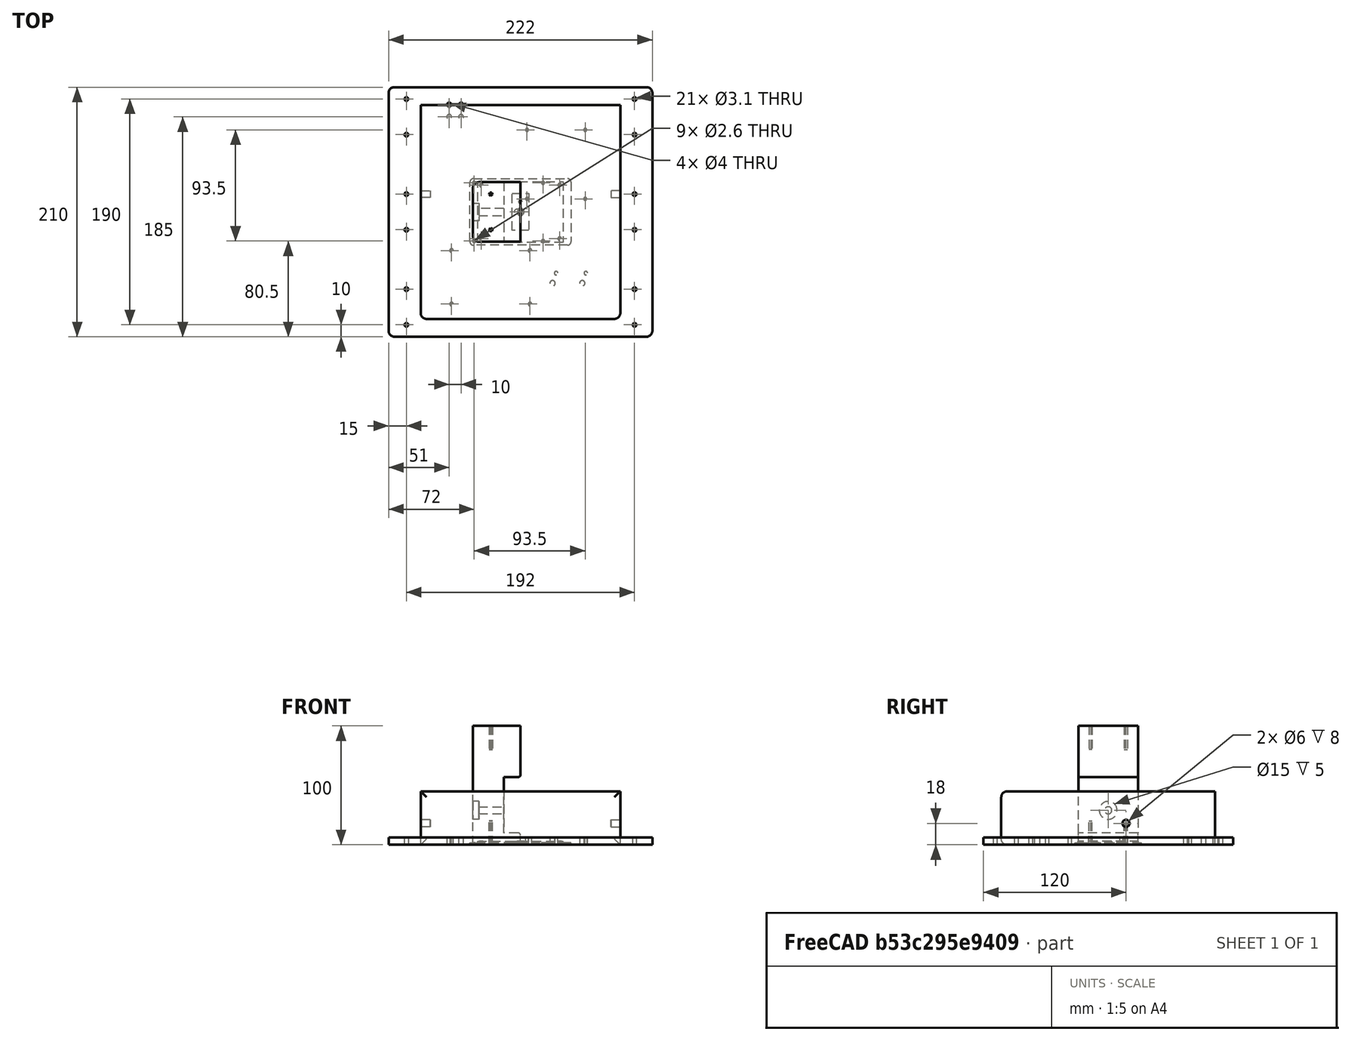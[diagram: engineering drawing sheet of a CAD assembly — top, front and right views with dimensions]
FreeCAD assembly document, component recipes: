
FREECAD ASSEMBLY — COMPONENT RECIPES ("case")

This assembly document has 11 components, labeled P0..P10 below (a component is one placed body or linked part). 10 of them carry a construction recipe — the FreeCAD feature program that regenerates the part from scratch, quoted from this document or its linked companion documents; the rest are supplied as boundary geometry only. No exploded tour is included for this assembly.
COMPONENT P0 — recipe-attached ("Upper_Panel", modeled in this document).
Construction recipe (the document's own serialized feature program — sketch geometry with constraints, then the solid features built on it; lengths are millimeters unless a unit is written):

FEATURE [PartDesign::FeatureBase] Clone
  BaseFeature = -> Lower_Panel
FEATURE [PartDesign::CoordinateSystem] Local_CS025
  AttacherType = Attacher::AttachEngine3D
  MapMode = 45
  Placement = pos=(-96,-80,0) rot=(0,0,1;0rad)
  Support = -> [Clone]
FEATURE [Sketcher::SketchObject] Sketch017
  AttachmentOffset = pos=(30,50,0) rot=(0,0,1;1.5708rad)
  FullyConstrained = true
  MapMode = 5
  Placement = pos=(30,50,0) rot=(0,0,1;1.5708rad)
  Support = -> [XY_Plane010]
  expr: .Constraints.hole_diameter = Sketch003.Constraints[3]
  expr: Constraints[34] = Sketch003.Constraints[34]
  expr: Constraints[36] = Sketch003.Constraints[36]
  expr: Constraints[12] = Sketch003.Constraints[12]
  expr: Constraints[13] = Sketch003.Constraints[13]
  expr: Constraints[31] = Sketch003.Constraints[31]
  expr: Constraints[35] = Sketch003.Constraints[35]
  sketch-geometry (16):
    g0: Circle CenterX=-39 CenterY=24.5 CenterZ=0 NormalX=0 NormalY=0 NormalZ=1 AngleXU=0 Radius=1.3
    g1: Circle CenterX=19 CenterY=24.5 CenterZ=0 NormalX=0 NormalY=0 NormalZ=1 AngleXU=0 Radius=1.3
    g2: Circle CenterX=-39 CenterY=-24.5 CenterZ=0 NormalX=0 NormalY=0 NormalZ=1 AngleXU=0 Radius=1.3
    g3: Circle CenterX=19 CenterY=-24.5 CenterZ=0 NormalX=0 NormalY=0 NormalZ=1 AngleXU=0 Radius=1.3
    g4: LineSegment StartX=-39 StartY=24.5 StartZ=0 EndX=19 EndY=24.5 EndZ=0
    g5: LineSegment StartX=19 StartY=24.5 StartZ=0 EndX=19 EndY=-24.5 EndZ=0
    g6: LineSegment StartX=19 StartY=-24.5 StartZ=0 EndX=-39 EndY=-24.5 EndZ=0
    g7: LineSegment StartX=-39 StartY=-24.5 StartZ=0 EndX=-39 EndY=24.5 EndZ=0
    g8: LineSegment StartX=-39.5 StartY=28 StartZ=0 EndX=39.5 EndY=28 EndZ=0
    g9: LineSegment StartX=42.5 StartY=25 StartZ=0 EndX=42.5 EndY=-25 EndZ=0
    g10: LineSegment StartX=39.5 StartY=-28 StartZ=0 EndX=-39.5 EndY=-28 EndZ=0
    g11: LineSegment StartX=-42.5 StartY=-25 StartZ=0 EndX=-42.5 EndY=25 EndZ=0
    g12: ArcOfCircle CenterX=-39.5 CenterY=25 CenterZ=0 NormalX=0 NormalY=0 NormalZ=1 AngleXU=0 Radius=3 StartAngle=1.5708 EndAngle=3.14159
    g13: ArcOfCircle CenterX=-39.5 CenterY=-25 CenterZ=0 NormalX=0 NormalY=0 NormalZ=1 AngleXU=0 Radius=3 StartAngle=3.14159 EndAngle=4.71239
    g14: ArcOfCircle CenterX=39.5 CenterY=-25 CenterZ=0 NormalX=0 NormalY=0 NormalZ=1 AngleXU=0 Radius=3 StartAngle=4.71239 EndAngle=6.28319
    g15: ArcOfCircle CenterX=39.5 CenterY=25 CenterZ=0 NormalX=0 NormalY=0 NormalZ=1 AngleXU=0 Radius=3 StartAngle=0 EndAngle=1.5708
  constraints (37):
    c: Equal(g0,g1)
    c: Equal(g1,g2)
    c: Equal(g2,g3)
    c: Diameter(g1) = 2.6  'hole_diameter'
    c: Coincident(g4,g5)
    c: Coincident(g5,g6)
    c: Coincident(g6,g7)
    c: Coincident(g7,g4)
    c: Horizontal(g4)
    c: Horizontal(g6)
    c: Vertical(g5)
    c: Symmetric(g4,g6,g-1)
    c: DistanceY(g7,g7) = 49
    c: DistanceX(g4,g4) = 58
    c: Coincident(g1,g4)
    c: Coincident(g3,g5)
    c: Coincident(g4,g0)
    c: Coincident(g6,g2)
    c: Horizontal(g8)
    c: Horizontal(g10)
    c: Vertical(g9)
    c: Vertical(g11)
    c: Tangent(g8,g12) = 1.5708
    c: Tangent(g11,g12) = 1.5708
    c: Tangent(g11,g13) = 1.5708
    c: Tangent(g10,g13) = 1.5708
    c: Tangent(g10,g14) = 1.5708
    c: Tangent(g9,g14) = 1.5708
    c: Tangent(g9,g15) = 1.5708
    c: Tangent(g8,g15) = 1.5708
    c: Equal(g13,g14)
    c: Radius(g15) = 3
    c: Symmetric(g8,g10,g-1)
    c: Symmetric(g11,g9,g-2)
    c: DistanceX(g11,g9) = 85
    c: DistanceY(g10,g8) = 56
    c: DistanceX(g11,g2) = 3.5
FEATURE [PartDesign::Pocket] Pocket009  label="Upper_Panel_Pi_Mounting_Holes"
  BaseFeature = -> Clone
  Length = 5
  Length2 = 100
  Profile = -> Sketch017
  Reversed = true
  Type = 1
FEATURE [PartDesign::CoordinateSystem] Local_CS026  label="Upper_Panel_Pi_Mounting_Hole_1"
  AttacherType = Attacher::AttachEngine3D
  AttachmentOffset = pos=(0,0,0) rot=(1,0,0;3.14159rad)
  MapMode = 45
  Placement = pos=(5.5,11,0) rot=(0.70712,0.707094,0;3.14159rad)
  Support = -> [Pocket009]
FEATURE [PartDesign::CoordinateSystem] Local_CS027  label="Upper_Panel_Pi_Mounting_Hole_2"
  AttacherType = Attacher::AttachEngine3D
  AttachmentOffset = pos=(0,0,0) rot=(1,0,0;3.14159rad)
  MapMode = 45
  Placement = pos=(54.5,11,0) rot=(0.70708,0.707133,0;3.14159rad)
  Support = -> [Pocket009]
FEATURE [PartDesign::CoordinateSystem] Local_CS028  label="Upper_Panel_Pi_Mounting_Hole_3"
  AttacherType = Attacher::AttachEngine3D
  AttachmentOffset = pos=(0,0,0) rot=(1,0,0;3.14159rad)
  MapMode = 45
  Placement = pos=(5.5,69,0) rot=(0.7071,0.707113,0;3.14159rad)
  Support = -> [Pocket009]
FEATURE [PartDesign::CoordinateSystem] Local_CS029  label="Upper_Panel_Pi_Mounting_Hole_4"
  AttacherType = Attacher::AttachEngine3D
  AttachmentOffset = pos=(0,0,0) rot=(1,0,0;3.14159rad)
  MapMode = 45
  Placement = pos=(54.5,69,0) rot=(0.707107,0.707107,0;3.14159rad)
  Support = -> [Pocket009]
FEATURE [Sketcher::SketchObject] Sketch018
  AttachmentOffset = pos=(-25,-55,0) rot=(0,0,1;0rad)
  FullyConstrained = true
  MapMode = 5
  Placement = pos=(-25,-55,0) rot=(0,0,1;0rad)
  Support = -> [XY_Plane010]
  expr: .Constraints.hole_diameter = Sketch001.Constraints[3]
  expr: Constraints[16] = Sketch001.Constraints[16]
  expr: Constraints[17] = Sketch001.Constraints[17]
  sketch-geometry (8):
    g0: Circle CenterX=-33 CenterY=22.5 CenterZ=0 NormalX=0 NormalY=0 NormalZ=1 AngleXU=0 Radius=1.55
    g1: Circle CenterX=33 CenterY=22.5 CenterZ=0 NormalX=0 NormalY=0 NormalZ=1 AngleXU=0 Radius=1.55
    g2: Circle CenterX=-33 CenterY=-22.5 CenterZ=0 NormalX=0 NormalY=0 NormalZ=1 AngleXU=0 Radius=1.55
    g3: Circle CenterX=33 CenterY=-22.5 CenterZ=0 NormalX=0 NormalY=0 NormalZ=1 AngleXU=0 Radius=1.55
    g4: LineSegment StartX=-33 StartY=22.5 StartZ=0 EndX=33 EndY=22.5 EndZ=0
    g5: LineSegment StartX=33 StartY=22.5 StartZ=0 EndX=33 EndY=-22.5 EndZ=0
    g6: LineSegment StartX=33 StartY=-22.5 StartZ=0 EndX=-33 EndY=-22.5 EndZ=0
    g7: LineSegment StartX=-33 StartY=-22.5 StartZ=0 EndX=-33 EndY=22.5 EndZ=0
  constraints (18):
    c: Equal(g0,g1)
    c: Equal(g1,g2)
    c: Equal(g2,g3)
    c: Diameter(g1) = 3.1  'hole_diameter'
    c: Coincident(g4,g5)
    c: Coincident(g5,g6)
    c: Coincident(g6,g7)
    c: Coincident(g7,g4)
    c: Horizontal(g6)
    c: Vertical(g5)
    c: Symmetric(g4,g6,g-1)
    c: Symmetric(g4,g4,g-2)
    c: Coincident(g0,g4)
    c: Coincident(g2,g6)
    c: Coincident(g1,g4)
    c: Coincident(g3,g5)
    c: DistanceX(g4,g4) = 66
    c: DistanceY(g7,g7) = 45
FEATURE [PartDesign::Pocket] Pocket010  label="Upper_Panel_Relay_Mounting_Holes"
  BaseFeature = -> Pocket009
  Length = 5
  Length2 = 100
  Profile = -> Sketch018
  Reversed = true
  Type = 1
FEATURE [PartDesign::CoordinateSystem] Local_CS030  label="Upper_Panel_Relay_Mounting_Hole_1"
  AttacherType = Attacher::AttachEngine3D
  AttachmentOffset = pos=(0,0,0) rot=(1,0,0;3.14159rad)
  MapMode = 45
  Placement = pos=(8,-77.5,0) rot=(1,6e-06,0;3.14159rad)
  Support = -> [Pocket010]
FEATURE [PartDesign::CoordinateSystem] Local_CS031  label="Upper_Panel_Relay_Mounting_Hole_2"
  AttacherType = Attacher::AttachEngine3D
  AttachmentOffset = pos=(0,0,0) rot=(1,0,0;3.14159rad)
  MapMode = 45
  Placement = pos=(8,-32.5,0) rot=(1,0,0;3.14159rad)
  Support = -> [Pocket010]
FEATURE [PartDesign::CoordinateSystem] Local_CS032  label="Upper_Panel_Relay_Mounting_Hole_3"
  AttacherType = Attacher::AttachEngine3D
  AttachmentOffset = pos=(0,0,0) rot=(1,0,0;3.14159rad)
  MapMode = 45
  Placement = pos=(-58,-77.5,0) rot=(1,-4.4e-05,0;3.14159rad)
  Support = -> [Pocket010]
FEATURE [PartDesign::CoordinateSystem] Local_CS033  label="Upper_Panel_Relay_Mounting_Hole_4"
  AttacherType = Attacher::AttachEngine3D
  AttachmentOffset = pos=(0,0,0) rot=(1,0,0;3.14159rad)
  MapMode = 45
  Placement = pos=(-58,-32.5,0) rot=(1,0,0;3.14159rad)
  Support = -> [Pocket010]
FEATURE [Sketcher::SketchObject] Sketch019
  FullyConstrained = true
  MapMode = 5
  Support = -> [XY_Plane010]
  expr: Constraints[18] = <<Lower_Panel_Outline>>.Constraints.depth / 2 - 15mm
  sketch-geometry (8):
    g0: Circle CenterX=-60 CenterY=90 CenterZ=0 NormalX=0 NormalY=0 NormalZ=1 AngleXU=0 Radius=2
    g1: Circle CenterX=-50 CenterY=90 CenterZ=0 NormalX=0 NormalY=0 NormalZ=1 AngleXU=0 Radius=2
    g2: Circle CenterX=-60 CenterY=80 CenterZ=0 NormalX=0 NormalY=0 NormalZ=1 AngleXU=0 Radius=2
    g3: Circle CenterX=-50 CenterY=80 CenterZ=0 NormalX=0 NormalY=0 NormalZ=1 AngleXU=0 Radius=2
    g4: LineSegment StartX=-60 StartY=90 StartZ=0 EndX=-50 EndY=90 EndZ=0
    g5: LineSegment StartX=-50 StartY=90 StartZ=0 EndX=-50 EndY=80 EndZ=0
    g6: LineSegment StartX=-50 StartY=80 StartZ=0 EndX=-60 EndY=80 EndZ=0
    g7: LineSegment StartX=-60 StartY=80 StartZ=0 EndX=-60 EndY=90 EndZ=0
  constraints (20):
    c: Equal(g0,g1)
    c: Equal(g1,g2)
    c: Equal(g2,g3)
    c: Coincident(g4,g5)
    c: Coincident(g5,g6)
    c: Coincident(g6,g7)
    c: Coincident(g7,g4)
    c: Horizontal(g4)
    c: Horizontal(g6)
    c: Vertical(g5)
    c: Vertical(g7)
    c: Coincident(g0,g4)
    c: Coincident(g4,g1)
    c: Coincident(g6,g2)
    c: Coincident(g5,g3)
    c: Diameter(g1) = 4
    c: Equal(g4,g7)
    c: DistanceY(g7,g7) = 10
    c: DistanceY(g-1,g1) = 90
    c: DistanceX(g3,g-1) = 50
FEATURE [PartDesign::Pocket] Pocket011  label="Upper_Panel_Cable_Clamp"
  BaseFeature = -> Pocket010
  Length = 5
  Length2 = 100
  Profile = -> Sketch019
  Reversed = true
  Type = 1
FEATURE [Sketcher::SketchObject] Sketch023  label="Photosensor_PCB_Mount_S"
  AttachmentOffset = pos=(30,-60,0) rot=(0,0,1;0rad)
  FullyConstrained = true
  MapMode = 5
  Placement = pos=(30,-60,0) rot=(0,0,1;0rad)
  Support = -> [XY_Plane010]
  expr: Constraints[24] = Sketch022.Constraints[11]
  expr: Constraints[25] = Sketch022.Constraints[12]
  expr: Constraints[21] = Sketch022.Constraints[8]
  expr: .Constraints.diameter = Sketch021.Constraints[12]
  expr: Constraints[11] = Sketch021.Constraints[11]
  expr: Constraints[22] = Sketch022.Constraints[9]
  expr: Constraints[9] = Sketch021.Constraints[9]
  expr: Constraints[8] = Sketch021.Constraints[8]
  sketch-geometry (10):
    g0: LineSegment StartX=-7 StartY=15.5 StartZ=0 EndX=7 EndY=15.5 EndZ=0
    g1: LineSegment StartX=7 StartY=15.5 StartZ=0 EndX=7 EndY=-15.5 EndZ=0
    g2: LineSegment StartX=7 StartY=-15.5 StartZ=0 EndX=-7 EndY=-15.5 EndZ=0
    g3: LineSegment StartX=-7 StartY=-15.5 StartZ=0 EndX=-7 EndY=15.5 EndZ=0
    g4: Circle CenterX=0 CenterY=8.5 CenterZ=0 NormalX=0 NormalY=0 NormalZ=1 AngleXU=0 Radius=1.5
    g5: LineSegment StartX=-7 StartY=15.5 StartZ=0 EndX=7 EndY=15.5 EndZ=0
    g6: LineSegment StartX=7 StartY=15.5 StartZ=0 EndX=7 EndY=-15.5 EndZ=0
    g7: LineSegment StartX=7 StartY=-15.5 StartZ=0 EndX=-7 EndY=-15.5 EndZ=0
    g8: LineSegment StartX=-7 StartY=-15.5 StartZ=0 EndX=-7 EndY=15.5 EndZ=0
    g9: Circle CenterX=-3 CenterY=0 CenterZ=0 NormalX=0 NormalY=0 NormalZ=1 AngleXU=0 Radius=2.25
  constraints (26):
    c: Coincident(g0,g1)
    c: Coincident(g1,g2)
    c: Coincident(g2,g3)
    c: Coincident(g3,g0)
    c: Horizontal(g2)
    c: Vertical(g1)
    c: Symmetric(g0,g0,g-2)
    c: Symmetric(g0,g2,g-1)
    c: DistanceX(g0,g0) = 14
    c: DistanceY(g1,g1) = 31
    c: PointOnObject(g4,g-2)
    c: DistanceY(g4,g0) = 7
    c: Diameter(g4) = 3  'diameter'
    c: Coincident(g5,g6)
    c: Coincident(g6,g7)
    c: Coincident(g7,g8)
    c: Coincident(g8,g5)
    c: Horizontal(g7)
    c: Vertical(g6)
    c: Symmetric(g5,g5,g-2)
    c: Symmetric(g5,g7,g-1)
    c: DistanceX(g5,g5) = 14
    c: DistanceY(g6,g6) = 31
    c: PointOnObject(g9,g-1)
    c: DistanceX(g9,g-1) = 3
    c: Diameter(g9) = 4.5
FEATURE [PartDesign::Pocket] Pocket013  label="Photosensor_PCB_Mount"
  BaseFeature = -> Pocket011
  Length = 0
  Length2 = 100
  Profile = -> Sketch023
  Reversed = true
  Type = 1
FEATURE [PartDesign::LinearPattern] LinearPattern  label="Photosensor_PCB_Mounts"
  BaseFeature = -> Pocket013
  Direction = -> Sketch023 [H_Axis]
  Length = 25
  Occurrences = 2
  Originals = -> [Pocket013]
FEATURE [PartDesign::CoordinateSystem] Local_CS035  label="Photosensor_PCB_1_Mounting_Hole"
  AttacherType = Attacher::AttachEngine3D
  MapMode = 45
  Placement = pos=(30,-51.5,0) rot=(0,0,1;0rad)
  Support = -> [LinearPattern]
FEATURE [PartDesign::CoordinateSystem] Local_CS036  label="Photosensor_PCB_2_Mounting_Hole"
  AttacherType = Attacher::AttachEngine3D
  MapMode = 45
  Placement = pos=(55,-51.5,0) rot=(0,0,1;0rad)
  Support = -> [LinearPattern]
FEATURE [PartDesign::Body] Body  label="Upper_Panel"
  BaseFeature = -> Lower_Panel
  Group = -> [Clone,Local_CS025,Sketch017,Pocket009,Local_CS026,Local_CS027,Local_CS028,Local_CS029,Sketch018,Pocket010,Local_CS030,Local_CS031,Local_CS032,Local_CS033,Sketch019,Pocket011,Sketch023,Pocket013,LinearPattern,Local_CS035,Local_CS036]
  Origin = -> Origin010
  Tip = -> LinearPattern
COMPONENT P1 — recipe-attached ("Pillar_Radio_Mount", modeled in this document).
Construction recipe (the document's own serialized feature program — sketch geometry with constraints, then the solid features built on it; lengths are millimeters unless a unit is written):

FEATURE [PartDesign::FeatureBase] Clone001
  BaseFeature = -> Corner_Pillar
FEATURE [Sketcher::SketchObject] Sketch024
  FullyConstrained = true
  MapMode = 5
  Placement = pos=(0,0,0) rot=(0.57735,0.57735,0.57735;2.0944rad)
  Support = -> [YZ_Plane013]
  sketch-geometry (1):
    g0: Circle CenterX=0 CenterY=29 CenterZ=0 NormalX=0 NormalY=0 NormalZ=1 AngleXU=0 Radius=3
  constraints (3):
    c: PointOnObject(g0,g-2)
    c: Diameter(g0) = 6
    c: DistanceY(g-1,g0) = 29
FEATURE [PartDesign::Plane] DatumPlane006  label="Pillar_Radio_Mount_Outer_Face"
  AttachmentOffset = pos=(0,0,-40) rot=(0,0,1;0rad)
  Length = 65.8114
  MapMode = 5
  Placement = pos=(-40,8.9e-15,-8.9e-15) rot=(0.57735,0.57735,0.57735;2.0944rad)
  ResizeMode = 0
  Support = -> [YZ_Plane013]
  Width = 140.811
  expr: .AttachmentOffset.Base.z = -<<Sketch010>>.Constraints.width
FEATURE [PartDesign::Pocket] Pocket014  label="Pillar_Radio_Mount_Hole"
  BaseFeature = -> Clone001
  Length = 0
  Length2 = 100
  Profile = -> Sketch024
  Type = 3
  UpToFace = -> DatumPlane006 [Plane]
FEATURE [PartDesign::CoordinateSystem] Local_CS037  label="Pillar_Radio_Mount_Hole_Pos"
  AttacherType = Attacher::AttachEngine3D
  MapMode = 45
  Placement = pos=(-14,2.37e-14,29) rot=(0.57735,0.57735,0.57735;2.0944rad)
  Support = -> [Pocket014]
FEATURE [Sketcher::SketchObject] Sketch025
  ExternalGeometry = -> [Pocket014]
  FullyConstrained = true
  MapMode = 5
  Placement = pos=(-40,8.9e-15,-8.9e-15) rot=(0.57735,0.57735,0.57735;2.0944rad)
  Support = -> [DatumPlane006]
  sketch-geometry (1):
    g0: Circle CenterX=8.9e-15 CenterY=29 CenterZ=0 NormalX=0 NormalY=0 NormalZ=1 AngleXU=0 Radius=7.5
  constraints (2):
    c: Coincident(g0,g-3)
    c: Diameter(g0) = 15
FEATURE [PartDesign::Pocket] Pocket015  label="Pillar_Radio_Mount_Hole_Recess"
  BaseFeature = -> Pocket014
  Length = 5
  Length2 = 100
  Profile = -> Sketch025
  Reversed = true
  Type = 0
FEATURE [PartDesign::CoordinateSystem] Local_CS038  label="Pillar_Radio_Mount_Mounting_Holes_Bottom_Pos"
  AttacherType = Attacher::AttachEngine3D
  AttachmentOffset = pos=(0,0,0) rot=(0,0.707107,0.707107;3.14159rad)
  MapMode = 45
  Placement = pos=(-25,0,0) rot=(0,0,1;0rad)
  Support = -> [Pocket015]
FEATURE [PartDesign::Body] Body001  label="Pillar_Radio_Mount"
  BaseFeature = -> Corner_Pillar
  Group = -> [Clone001,DatumPlane006,Sketch024,Pocket014,Local_CS037,Sketch025,Pocket015,Local_CS038]
  Origin = -> Origin013
  Tip = -> Pocket015
COMPONENT P2 — recipe-attached ("Pillar", modeled in this document).
Construction recipe (the document's own serialized feature program — sketch geometry with constraints, then the solid features built on it; lengths are millimeters unless a unit is written):

FEATURE [Sketcher::SketchObject] Sketch010
  FullyConstrained = true
  MapMode = 5
  Support = -> [XY_Plane008]
  expr: Constraints[9] = <<Lower_Panel_Outline>>.Constraints.corner_radius
  sketch-geometry (6):
    g0: LineSegment StartX=-35 StartY=25 StartZ=0 EndX=0 EndY=25 EndZ=0
    g1: LineSegment StartX=0 StartY=25 StartZ=0 EndX=0 EndY=-25 EndZ=0
    g2: LineSegment StartX=0 StartY=-25 StartZ=0 EndX=-35 EndY=-25 EndZ=0
    g3: LineSegment StartX=-40 StartY=-20 StartZ=0 EndX=-40 EndY=20 EndZ=0
    g4: ArcOfCircle CenterX=-35 CenterY=20 CenterZ=0 NormalX=0 NormalY=0 NormalZ=1 AngleXU=0 Radius=5 StartAngle=1.5708 EndAngle=3.14159
    g5: ArcOfCircle CenterX=-35 CenterY=-20 CenterZ=0 NormalX=0 NormalY=0 NormalZ=1 AngleXU=0 Radius=5 StartAngle=3.14159 EndAngle=4.71239
  constraints (15):
    c: Coincident(g0,g1)
    c: Coincident(g1,g2)
    c: Horizontal(g2)
    c: Vertical(g3)
    c: Tangent(g0,g4) = 1.5708
    c: Tangent(g3,g4) = 1.5708
    c: Tangent(g3,g5) = 1.5708
    c: Tangent(g2,g5) = 1.5708
    c: Equal(g4,g5)
    c: Radius(g4) = 5
    c: Symmetric(g0,g1,g-1)
    c: DistanceY(g1,g1) = 50  'depth'
    c: DistanceX(g3,g1) = 40  'width'
    c: PointOnObject(g1,g-2)
    c: Horizontal(g0)
FEATURE [PartDesign::Plane] DatumPlane003  label="Pillar_Top_Face"
  AttachmentOffset = pos=(0,0,100) rot=(0,0,1;0rad)
  Length = 76.4018
  MapMode = 5
  Placement = pos=(0,0,100) rot=(0,0,1;0rad)
  ResizeMode = 0
  Support = -> [XY_Plane008]
  Width = 61.4018
FEATURE [PartDesign::Pad] Pad007  label="Pillar_Body"
  Direction = (1,1,1)
  Length = 10
  Length2 = 100
  Profile = -> Sketch010
  Type = 3
  UpToFace = -> DatumPlane003 [Plane]
FEATURE [Sketcher::SketchObject] Sketch011
  ExternalGeometry = -> [Pad007]
  FullyConstrained = true
  MapMode = 5
  Placement = pos=(0,0,0) rot=(0.57735,0.57735,0.57735;2.0944rad)
  Support = -> [YZ_Plane008]
  expr: Constraints[11] = <<Motorola_GM900_Body>>.Length + 2mm
  sketch-geometry (4):
    g0: LineSegment StartX=-25 StartY=57 StartZ=0 EndX=25 EndY=57 EndZ=0
    g1: LineSegment StartX=25 StartY=57 StartZ=0 EndX=25 EndY=10 EndZ=0
    g2: LineSegment StartX=25 StartY=10 StartZ=0 EndX=-25 EndY=10 EndZ=0
    g3: LineSegment StartX=-25 StartY=10 StartZ=0 EndX=-25 EndY=57 EndZ=0
  constraints (13):
    c: Coincident(g0,g1)
    c: Coincident(g1,g2)
    c: Coincident(g2,g3)
    c: Coincident(g3,g0)
    c: Horizontal(g0)
    c: Horizontal(g2)
    c: Vertical(g1)
    c: Vertical(g3)
    c: PointOnObject(g0,g-3)
    c: PointOnObject(g0,g-4)
    c: DistanceY(g-1,g1) = 10  'lower_y_offset'
    c: DistanceY(g3,g3) = 47
    c: DistanceY(g0,g-4) = 43
FEATURE [PartDesign::Pocket] Pocket003  label="Pillar_Radio_Cutout"
  BaseFeature = -> Pad007
  Length = 14
  Length2 = 100
  Profile = -> Sketch011
  Type = 0
FEATURE [Sketcher::SketchObject] Sketch012
  ExternalGeometry = -> [Sketch010]
  FullyConstrained = true
  MapMode = 5
  Support = -> [XY_Plane008]
  sketch-geometry (13):
    g0: LineSegment StartX=-25 StartY=15 StartZ=0 EndX=-25 EndY=-15 EndZ=0
    g1: LineSegment StartX=-25 StartY=13.475 StartZ=0 EndX=-23.5496 EndY=14.5287 EndZ=0
    g2: LineSegment StartX=-23.5496 StartY=14.5287 StartZ=0 EndX=-24.1036 EndY=16.2338 EndZ=0
    g3: LineSegment StartX=-24.1036 StartY=16.2338 StartZ=0 EndX=-25.8964 EndY=16.2338 EndZ=0
    g4: LineSegment StartX=-25.8964 StartY=16.2338 StartZ=0 EndX=-26.4504 EndY=14.5287 EndZ=0
    g5: LineSegment StartX=-26.4504 StartY=14.5287 StartZ=0 EndX=-25 EndY=13.475 EndZ=0
    g6: Circle CenterX=-25 CenterY=15 CenterZ=0 NormalX=0 NormalY=0 NormalZ=1 AngleXU=0 Radius=1.525
    g7: LineSegment StartX=-25 StartY=-13.475 StartZ=0 EndX=-26.4504 EndY=-14.5287 EndZ=0
    g8: LineSegment StartX=-26.4504 StartY=-14.5287 StartZ=0 EndX=-25.8964 EndY=-16.2338 EndZ=0
    g9: LineSegment StartX=-25.8964 StartY=-16.2338 StartZ=0 EndX=-24.1036 EndY=-16.2338 EndZ=0
    g10: LineSegment StartX=-24.1036 StartY=-16.2338 StartZ=0 EndX=-23.5496 EndY=-14.5287 EndZ=0
    g11: LineSegment StartX=-23.5496 StartY=-14.5287 StartZ=0 EndX=-25 EndY=-13.475 EndZ=0
    g12: Circle CenterX=-25 CenterY=-15 CenterZ=0 NormalX=0 NormalY=0 NormalZ=1 AngleXU=0 Radius=1.525
  constraints (33):
    c: DistanceY(g0,g0) = 30  'between_centres'
    c: DistanceX(g-3,g0) = 10
    c: Symmetric(g0,g0,g-1)
    c: Coincident(g1,g2)
    c: Coincident(g2,g3)
    c: Coincident(g3,g4)
    c: Coincident(g4,g5)
    c: Coincident(g5,g1)
    c: Equal(g1, g2-g5) x4
    c: PointOnObject(g1,g6)
    c: PointOnObject(g2,g6)
    c: PointOnObject(g3,g6)
    c: PointOnObject(g4,g6)
    c: PointOnObject(g5,g6)
    c: Coincident(g6,g0)
    c: PointOnObject(g5,g0)
    c: Coincident(g7,g8)
    c: Coincident(g8,g9)
    c: Coincident(g9,g10)
    c: Coincident(g10,g11)
    c: Coincident(g11,g7)
    c: Equal(g7, g8-g11) x4
    c: PointOnObject(g7,g12)
    c: PointOnObject(g8,g12)
    c: PointOnObject(g9,g12)
    c: PointOnObject(g10,g12)
    c: PointOnObject(g11,g12)
    c: Coincident(g12,g0)
    c: PointOnObject(g11,g0)
    c: Equal(g6,g12)
    c: Diameter(g6) = 3.05
    c: DistanceX(g-5,g0) = 15  'x_offset'
    c: DistanceY(g-6,g0) = 10  'y_offset'
FEATURE [Sketcher::SketchObject] Sketch013
  ExternalGeometry = -> [Sketch010]
  FullyConstrained = true
  MapMode = 5
  Placement = pos=(0,0,100) rot=(0,0,1;0rad)
  Support = -> [DatumPlane003]
  expr: Constraints[38] = Sketch012.Constraints[36]
  expr: Constraints[3] = Sketch012.Constraints[1]
  expr: Constraints[0] = Sketch012.Constraints.between_centres
  sketch-geometry (13):
    g0: LineSegment StartX=-25 StartY=15 StartZ=0 EndX=-25 EndY=-15 EndZ=0
    g1: LineSegment StartX=-25 StartY=13.475 StartZ=0 EndX=-23.5496 EndY=14.5287 EndZ=0
    g2: LineSegment StartX=-23.5496 StartY=14.5287 StartZ=0 EndX=-24.1036 EndY=16.2338 EndZ=0
    g3: LineSegment StartX=-24.1036 StartY=16.2338 StartZ=0 EndX=-25.8964 EndY=16.2338 EndZ=0
    g4: LineSegment StartX=-25.8964 StartY=16.2338 StartZ=0 EndX=-26.4504 EndY=14.5287 EndZ=0
    g5: LineSegment StartX=-26.4504 StartY=14.5287 StartZ=0 EndX=-25 EndY=13.475 EndZ=0
    g6: Circle CenterX=-25 CenterY=15 CenterZ=0 NormalX=0 NormalY=0 NormalZ=1 AngleXU=0 Radius=1.525
    g7: LineSegment StartX=-25 StartY=-13.475 StartZ=0 EndX=-26.4504 EndY=-14.5287 EndZ=0
    g8: LineSegment StartX=-26.4504 StartY=-14.5287 StartZ=0 EndX=-25.8964 EndY=-16.2338 EndZ=0
    g9: LineSegment StartX=-25.8964 StartY=-16.2338 StartZ=0 EndX=-24.1036 EndY=-16.2338 EndZ=0
    g10: LineSegment StartX=-24.1036 StartY=-16.2338 StartZ=0 EndX=-23.5496 EndY=-14.5287 EndZ=0
    g11: LineSegment StartX=-23.5496 StartY=-14.5287 StartZ=0 EndX=-25 EndY=-13.475 EndZ=0
    g12: Circle CenterX=-25 CenterY=-15 CenterZ=0 NormalX=0 NormalY=0 NormalZ=1 AngleXU=0 Radius=1.525
  constraints (33):
    c: DistanceY(g0,g0) = 30
    c: DistanceY(g-5,g0) = 5
    c: DistanceY(g0,g-3) = 5
    c: DistanceX(g-3,g0) = 10
    c: Symmetric(g0,g0,g-1)
    c: Coincident(g1,g2)
    c: Coincident(g2,g3)
    c: Coincident(g3,g4)
    c: Coincident(g4,g5)
    c: Coincident(g5,g1)
    c: Equal(g1, g2-g5) x4
    c: PointOnObject(g1,g6)
    c: PointOnObject(g2,g6)
    c: PointOnObject(g3,g6)
    c: PointOnObject(g4,g6)
    c: PointOnObject(g5,g6)
    c: Coincident(g6,g0)
    c: PointOnObject(g5,g0)
    c: Coincident(g7,g8)
    c: Coincident(g8,g9)
    c: Coincident(g9,g10)
    c: Coincident(g10,g11)
    c: Coincident(g11,g7)
    c: Equal(g7, g8-g11) x4
    c: PointOnObject(g7,g12)
    c: PointOnObject(g8,g12)
    c: PointOnObject(g9,g12)
    c: PointOnObject(g10,g12)
    c: PointOnObject(g11,g12)
    c: Coincident(g12,g0)
    c: PointOnObject(g11,g0)
    c: Equal(g6,g12)
    c: Diameter(g6) = 3.05
FEATURE [PartDesign::Fillet] Fillet  label="Pillar_Radio_Cutout_Rounding"
  Base = -> Pocket003 [Edge28,Edge23]
  BaseFeature = -> Pocket003
  Radius = 2
  SupportTransform = false
FEATURE [PartDesign::Pocket] Pocket004  label="Pillar_Bottom_Holes"
  BaseFeature = -> Fillet
  Length = 20
  Length2 = 100
  Profile = -> Sketch012
  Reversed = true
  Type = 0
FEATURE [PartDesign::Pocket] Pocket005  label="Pillar_Top_Holes"
  BaseFeature = -> Pocket004
  Length = 20
  Length2 = 100
  Profile = -> Sketch013
  Type = 0
  expr: Length = Pocket004.Length
FEATURE [PartDesign::CoordinateSystem] Local_CS014  label="Pillar_Mounting_Holes_Top_Pos"
  AttacherType = Attacher::AttachEngine3D
  AttachmentOffset = pos=(0,0,0) rot=(0,0.707107,0.707107;3.14159rad)
  MapMode = 45
  Placement = pos=(-25,0,100) rot=(0,0,1;0rad)
  Support = -> [Pocket005]
FEATURE [PartDesign::CoordinateSystem] Local_CS016  label="Pillar_Mounting_Holes_Bottom_Pos"
  AttacherType = Attacher::AttachEngine3D
  AttachmentOffset = pos=(0,0,0) rot=(0,0.707107,0.707107;3.14159rad)
  MapMode = 45
  Placement = pos=(-25,0,0) rot=(0,0,1;0rad)
  Support = -> [Pocket005]
FEATURE [PartDesign::Body] Corner_Pillar  label="Pillar"
  Group = -> [Sketch010,DatumPlane003,Pad007,Sketch011,Pocket003,Fillet,Sketch012,Pocket004,Sketch013,Pocket005,Local_CS014,Local_CS016]
  Origin = -> Origin008
  Tip = -> Pocket005
COMPONENT P3 — recipe-attached ("Lower_Panel", modeled in this document).
Construction recipe (the document's own serialized feature program — sketch geometry with constraints, then the solid features built on it; lengths are millimeters unless a unit is written):

FEATURE [PartDesign::CoordinateSystem] LCS_0
  AttacherType = Attacher::AttachEngine3D
  MapMode = 2
  Support = -> [X_Axis007]
FEATURE [Sketcher::SketchObject] Sketch009  label="Lower_Panel_Outline"
  FullyConstrained = true
  MapMode = 5
  Support = -> [XY_Plane007]
  expr: .Constraints.width = Sketch004.Constraints.width + 2 * (40mm - 14mm) + 2mm
  sketch-geometry (8):
    g0: LineSegment StartX=-106 StartY=105 StartZ=0 EndX=106 EndY=105 EndZ=0
    g1: LineSegment StartX=111 StartY=100 StartZ=0 EndX=111 EndY=-100 EndZ=0
    g2: LineSegment StartX=106 StartY=-105 StartZ=0 EndX=-106 EndY=-105 EndZ=0
    g3: LineSegment StartX=-111 StartY=-100 StartZ=0 EndX=-111 EndY=100 EndZ=0
    g4: ArcOfCircle CenterX=-106 CenterY=100 CenterZ=0 NormalX=0 NormalY=0 NormalZ=1 AngleXU=0 Radius=5 StartAngle=1.5708 EndAngle=3.14159
    g5: ArcOfCircle CenterX=106 CenterY=100 CenterZ=0 NormalX=0 NormalY=0 NormalZ=1 AngleXU=0 Radius=5 StartAngle=-9e-16 EndAngle=1.5708
    g6: ArcOfCircle CenterX=106 CenterY=-100 CenterZ=0 NormalX=0 NormalY=0 NormalZ=1 AngleXU=0 Radius=5 StartAngle=4.71239 EndAngle=6.28319
    g7: ArcOfCircle CenterX=-106 CenterY=-100 CenterZ=0 NormalX=0 NormalY=0 NormalZ=1 AngleXU=0 Radius=5 StartAngle=3.14159 EndAngle=4.71239
  constraints (18):
    c: Horizontal(g0)
    c: Horizontal(g2)
    c: Vertical(g1)
    c: Vertical(g3)
    c: Tangent(g0,g4) = 1.5708
    c: Tangent(g3,g4) = 1.5708
    c: Tangent(g0,g5) = 1.5708
    c: Tangent(g1,g5) = 1.5708
    c: Tangent(g1,g6) = 1.5708
    c: Tangent(g2,g6) = 1.5708
    c: Tangent(g3,g7) = 1.5708
    c: Tangent(g2,g7) = 1.5708
    c: Equal(g5,g6)
    c: Radius(g5) = 5  'corner_radius'
    c: Symmetric(g4,g7,g-1)
    c: Symmetric(g4,g5,g-2)
    c: DistanceX(g3,g1) = 222  'width'
    c: DistanceY(g2,g0) = 210  'depth'
FEATURE [PartDesign::Plane] DatumPlane002  label="Lower_Panel_Top_Face"
  AttachmentOffset = pos=(0,0,6) rot=(0,0,1;0rad)
  Length = 60
  MapMode = 5
  Placement = pos=(0,0,6) rot=(0,0,1;0rad)
  ResizeMode = 0
  Support = -> [XY_Plane007]
  Width = 60
FEATURE [PartDesign::Pad] Pad006  label="Lower_Panel_Panel"
  Direction = (1,1,1)
  Length = 10
  Length2 = 100
  Profile = -> Sketch009
  Type = 3
  UpToFace = -> DatumPlane002 [Plane]
FEATURE [Sketcher::SketchObject] Sketch015
  FullyConstrained = true
  MapMode = 5
  Placement = pos=(0,0,6) rot=(0,0,1;0rad)
  Support = -> [DatumPlane002]
  expr: Constraints[40] = <<Sketch012>>.Constraints.between_centres
  expr: Constraints[41] = <<Sketch012>>.Constraints.between_centres
  expr: Constraints[42] = <<Sketch012>>.Constraints.between_centres
  expr: .Constraints.corner_radius = Sketch009.Constraints[13]
  expr: .Constraints.width = Sketch009.Constraints[16]
  expr: .Constraints.depth = Sketch009.Constraints[17]
  expr: Constraints[62] = Sketch012.Constraints.x_offset
  expr: Constraints[63] = Sketch012.Constraints.y_offset
  sketch-geometry (28):
    g0: Circle CenterX=-96 CenterY=95 CenterZ=0 NormalX=0 NormalY=0 NormalZ=1 AngleXU=0 Radius=1.55
    g1: Circle CenterX=-96 CenterY=65 CenterZ=0 NormalX=0 NormalY=0 NormalZ=1 AngleXU=0 Radius=1.55
    g2: Circle CenterX=-96 CenterY=15 CenterZ=0 NormalX=0 NormalY=0 NormalZ=1 AngleXU=0 Radius=1.55
    g3: Circle CenterX=-96 CenterY=-15 CenterZ=0 NormalX=0 NormalY=0 NormalZ=1 AngleXU=0 Radius=1.55
    g4: Circle CenterX=-96 CenterY=-65 CenterZ=0 NormalX=0 NormalY=0 NormalZ=1 AngleXU=0 Radius=1.55
    g5: Circle CenterX=-96 CenterY=-95 CenterZ=0 NormalX=0 NormalY=0 NormalZ=1 AngleXU=0 Radius=1.55
    g6: Circle CenterX=96 CenterY=95 CenterZ=0 NormalX=0 NormalY=0 NormalZ=1 AngleXU=0 Radius=1.55
    g7: Circle CenterX=96 CenterY=65 CenterZ=0 NormalX=0 NormalY=0 NormalZ=1 AngleXU=0 Radius=1.55
    g8: Circle CenterX=96 CenterY=15 CenterZ=0 NormalX=0 NormalY=0 NormalZ=1 AngleXU=0 Radius=1.55
    g9: Circle CenterX=96 CenterY=-15 CenterZ=0 NormalX=0 NormalY=0 NormalZ=1 AngleXU=0 Radius=1.55
    g10: Circle CenterX=96 CenterY=-65 CenterZ=0 NormalX=0 NormalY=0 NormalZ=1 AngleXU=0 Radius=1.55
    g11: Circle CenterX=96 CenterY=-95 CenterZ=0 NormalX=0 NormalY=0 NormalZ=1 AngleXU=0 Radius=1.55
    g12: LineSegment StartX=-96 StartY=95 StartZ=0 EndX=-96 EndY=-95 EndZ=0
    g13: LineSegment StartX=96 StartY=95 StartZ=0 EndX=96 EndY=-95 EndZ=0
    g14: LineSegment StartX=-96 StartY=95 StartZ=0 EndX=96 EndY=95 EndZ=0
    g15: LineSegment StartX=96 StartY=65 StartZ=0 EndX=-96 EndY=65 EndZ=0
    g16: LineSegment StartX=-96 StartY=15 StartZ=0 EndX=96 EndY=15 EndZ=0
    g17: LineSegment StartX=96 StartY=-15 StartZ=0 EndX=-96 EndY=-15 EndZ=0
    g18: LineSegment StartX=-96 StartY=-65 StartZ=0 EndX=96 EndY=-65 EndZ=0
    g19: LineSegment StartX=96 StartY=-95 StartZ=0 EndX=-96 EndY=-95 EndZ=0
    g20: LineSegment StartX=-106 StartY=105 StartZ=0 EndX=106 EndY=105 EndZ=0
    g21: LineSegment StartX=111 StartY=100 StartZ=0 EndX=111 EndY=-100 EndZ=0
    g22: LineSegment StartX=106 StartY=-105 StartZ=0 EndX=-106 EndY=-105 EndZ=0
    g23: LineSegment StartX=-111 StartY=-100 StartZ=0 EndX=-111 EndY=100 EndZ=0
    g24: ArcOfCircle CenterX=-106 CenterY=100 CenterZ=0 NormalX=0 NormalY=0 NormalZ=1 AngleXU=0 Radius=5 StartAngle=1.5708 EndAngle=3.14159
    g25: ArcOfCircle CenterX=106 CenterY=100 CenterZ=0 NormalX=0 NormalY=0 NormalZ=1 AngleXU=0 Radius=5 StartAngle=1.2e-15 EndAngle=1.5708
    g26: ArcOfCircle CenterX=106 CenterY=-100 CenterZ=0 NormalX=0 NormalY=0 NormalZ=1 AngleXU=0 Radius=5 StartAngle=4.71239 EndAngle=6.28319
    g27: ArcOfCircle CenterX=-106 CenterY=-100 CenterZ=0 NormalX=0 NormalY=0 NormalZ=1 AngleXU=0 Radius=5 StartAngle=3.14159 EndAngle=4.71239
  constraints (67):
    c: Vertical(g13)
    c: Horizontal(g14)
    c: Horizontal(g15)
    c: Horizontal(g16)
    c: Horizontal(g17)
    c: Coincident(g14,g12)
    c: PointOnObject(g15,g12)
    c: PointOnObject(g16,g12)
    c: PointOnObject(g18,g12)
    c: Coincident(g19,g12)
    c: Coincident(g13,g19)
    c: PointOnObject(g18,g13)
    c: PointOnObject(g17,g13)
    c: Coincident(g13,g14)
    c: PointOnObject(g15,g13)
    c: PointOnObject(g16,g13)
    c: Coincident(g0,g12)
    c: Coincident(g1,g15)
    c: Coincident(g16,g2)
    c: Coincident(g3,g17)
    c: Coincident(g4,g18)
    c: Horizontal(g18)
    c: Coincident(g5,g12)
    c: Coincident(g18,g10)
    c: Coincident(g7,g15)
    c: Coincident(g13,g6)
    c: Coincident(g8,g16)
    c: Coincident(g9,g17)
    c: Equal(g0,g1)
    c: Equal(g1,g2)
    c: Equal(g2,g3)
    c: Equal(g3,g4)
    c: Equal(g4,g5)
    c: Equal(g5,g6)
    c: Equal(g6,g7)
    c: Equal(g7,g8)
    c: Equal(g8,g9)
    c: Equal(g9,g10)
    c: Equal(g10,g11)
    c: Coincident(g13,g11)
    c: DistanceY(g1,g0) = 30
    c: DistanceY(g3,g2) = 30
    c: DistanceY(g5,g4) = 30
    c: Diameter(g6) = 3.1
    c: Horizontal(g20)
    c: Horizontal(g22)
    c: Vertical(g21)
    c: Vertical(g23)
    c: Tangent(g20,g24) = 1.5708
    c: Tangent(g23,g24) = 1.5708
    c: Tangent(g20,g25) = 1.5708
    c: Tangent(g21,g25) = 1.5708
    c: Tangent(g21,g26) = 1.5708
    c: Tangent(g22,g26) = 1.5708
    c: Tangent(g23,g27) = 1.5708
    c: Tangent(g22,g27) = 1.5708
    c: Equal(g25,g26)
    c: Radius(g25) = 5  'corner_radius'
    c: Symmetric(g24,g27,g-1)
    c: Symmetric(g24,g25,g-2)
    c: DistanceX(g23,g21) = 222  'width'
    c: DistanceY(g22,g20) = 210  'depth'
    c: DistanceX(g23,g5) = 15
    c: DistanceY(g22,g5) = 10
    c: Symmetric(g5,g11,g-2)
    c: Symmetric(g0,g5,g-1)
    c: Symmetric(g2,g3,g-1)
FEATURE [PartDesign::Pocket] Pocket007
  BaseFeature = -> Pad006
  Length = 0
  Length2 = 100
  Profile = -> Sketch015
  Type = 3
  UpToFace = -> XY_Plane007
FEATURE [PartDesign::CoordinateSystem] Local_CS019
  AttacherType = Attacher::AttachEngine3D
  MapMode = 45
  Placement = pos=(-96,80,6) rot=(0,0,1;0rad)
  Support = -> [Pocket007]
FEATURE [PartDesign::CoordinateSystem] Local_CS020
  AttacherType = Attacher::AttachEngine3D
  MapMode = 45
  Placement = pos=(-96,-1.5e-15,6) rot=(0,0,1;0rad)
  Support = -> [Pocket007]
FEATURE [PartDesign::CoordinateSystem] Local_CS021
  AttacherType = Attacher::AttachEngine3D
  MapMode = 45
  Placement = pos=(-96,-80,6) rot=(0,0,1;0rad)
  Support = -> [Pocket007]
FEATURE [PartDesign::CoordinateSystem] Local_CS022
  AttacherType = Attacher::AttachEngine3D
  MapMode = 45
  Placement = pos=(96,80,6) rot=(0,0,1;0rad)
  Support = -> [Pocket007]
FEATURE [PartDesign::CoordinateSystem] Local_CS023
  AttacherType = Attacher::AttachEngine3D
  MapMode = 45
  Placement = pos=(96,-1.5e-15,6) rot=(0,0,1;0rad)
  Support = -> [Pocket007]
FEATURE [PartDesign::CoordinateSystem] Local_CS024
  AttacherType = Attacher::AttachEngine3D
  MapMode = 45
  Placement = pos=(96,-80,6) rot=(0,0,1;0rad)
  Support = -> [Pocket007]
FEATURE [PartDesign::Body] Lower_Panel
  Group = -> [LCS_0,Sketch009,DatumPlane002,Pad006,Sketch015,Pocket007,Local_CS019,Local_CS020,Local_CS021,Local_CS022,Local_CS023,Local_CS024]
  Origin = -> Origin007
  Tip = -> Pocket007
COMPONENT P4 — geometry summary ("Model"; no construction recipe available for this part):
  bounding box: 222.0 x 210.0 x 112.0 mm
  tessellated surface: 36,356 triangles
  volume: 2925796 mm^3 (56% of its bounding box)
COMPONENT P5 — recipe-attached ("Motorola_GM900", modeled in this document).
Construction recipe (the document's own serialized feature program — sketch geometry with constraints, then the solid features built on it; lengths are millimeters unless a unit is written):

FEATURE [Sketcher::SketchObject] Sketch004
  FullyConstrained = true
  MapMode = 5
  Support = -> [XY_Plane003]
  sketch-geometry (4):
    g0: LineSegment StartX=-84 StartY=90 StartZ=0 EndX=84 EndY=90 EndZ=0
    g1: LineSegment StartX=84 StartY=90 StartZ=0 EndX=84 EndY=-90 EndZ=0
    g2: LineSegment StartX=84 StartY=-90 StartZ=0 EndX=-84 EndY=-90 EndZ=0
    g3: LineSegment StartX=-84 StartY=-90 StartZ=0 EndX=-84 EndY=90 EndZ=0
  constraints (10):
    c: Coincident(g0,g1)
    c: Coincident(g1,g2)
    c: Coincident(g2,g3)
    c: Coincident(g3,g0)
    c: Horizontal(g2)
    c: Vertical(g1)
    c: Symmetric(g0,g2,g-1)
    c: Symmetric(g0,g0,g-2)
    c: DistanceX(g0,g0) = 168  'width'
    c: DistanceY(g3,g3) = 180  'depth'
FEATURE [PartDesign::Pad] Pad002  label="Motorola_GM900_Body"
  Direction = (1,1,1)
  Length = 45
  Length2 = 100
  Profile = -> Sketch004
  Type = 0
FEATURE [Sketcher::SketchObject] Sketch005
  ExternalGeometry = -> [Pad002]
  FullyConstrained = true
  MapMode = 5
  Placement = pos=(84,0,0) rot=(0.57735,0.57735,0.57735;2.0944rad)
  Support = -> [Pad002]
  sketch-geometry (1):
    g0: Circle CenterX=15 CenterY=18 CenterZ=0 NormalX=0 NormalY=0 NormalZ=1 AngleXU=0 Radius=3
  constraints (3):
    c: DistanceX(g0,g-6) = 75
    c: DistanceY(g-6,g0) = 18  'y_offset'
    c: Diameter(g0) = 6
FEATURE [PartDesign::Pocket] Pocket002  label="Motorola_GM900_Mounting_Hole_Right"
  BaseFeature = -> Pad002
  Length = 8
  Length2 = 100
  Profile = -> Sketch005
  Type = 0
FEATURE [PartDesign::Mirrored] Mirrored  label="Motorola_GM900_Mounting_Hole_Left"
  BaseFeature = -> Pocket002
  MirrorPlane = -> YZ_Plane003
  Originals = -> [Pocket002]
FEATURE [PartDesign::CoordinateSystem] Local_CS001  label="Motorola_GM900_Mounting_Hole_Left_Pos"
  AttacherType = Attacher::AttachEngine3D
  MapMode = 45
  Placement = pos=(-84,15,18) rot=(0.57735,0.577351,0.57735;2.09439rad)
  Support = -> [Mirrored]
FEATURE [PartDesign::CoordinateSystem] Local_CS002  label="Motorola_GM900_Mounting_Hole_Right_Pos"
  AttacherType = Attacher::AttachEngine3D
  MapMode = 45
  Placement = pos=(84,15,18) rot=(0.57735,0.577351,0.57735;2.09439rad)
  Support = -> [Mirrored]
FEATURE [PartDesign::Fillet] Fillet001
  Base = -> Mirrored [Face6]
  BaseFeature = -> Mirrored
  Radius = 5
  SupportTransform = false
FEATURE [PartDesign::Body] Motorola_GM900
  Group = -> [Sketch004,Pad002,Sketch005,Pocket002,Mirrored,Local_CS001,Local_CS002,Fillet001]
  Origin = -> Origin003
  Tip = -> Fillet001
COMPONENT P6 — recipe-attached ("Photosensor_PCB", modeled in this document).
Construction recipe (the document's own serialized feature program — sketch geometry with constraints, then the solid features built on it; lengths are millimeters unless a unit is written):

FEATURE [Sketcher::SketchObject] Sketch020  label="Photosensor_PCB_PCB_S"
  FullyConstrained = true
  MapMode = 5
  Support = -> [XY_Plane011]
  sketch-geometry (4):
    g0: LineSegment StartX=-7 StartY=15.5 StartZ=0 EndX=7 EndY=15.5 EndZ=0
    g1: LineSegment StartX=7 StartY=15.5 StartZ=0 EndX=7 EndY=-15.5 EndZ=0
    g2: LineSegment StartX=7 StartY=-15.5 StartZ=0 EndX=-7 EndY=-15.5 EndZ=0
    g3: LineSegment StartX=-7 StartY=-15.5 StartZ=0 EndX=-7 EndY=15.5 EndZ=0
  constraints (10):
    c: Coincident(g0,g1)
    c: Coincident(g1,g2)
    c: Coincident(g2,g3)
    c: Coincident(g3,g0)
    c: Horizontal(g2)
    c: Vertical(g1)
    c: Symmetric(g0,g0,g-2)
    c: Symmetric(g0,g2,g-1)
    c: DistanceX(g0,g0) = 14
    c: DistanceY(g1,g1) = 31
FEATURE [PartDesign::Plane] DatumPlane005
  AttachmentOffset = pos=(0,0,1.6) rot=(0,0,1;0rad)
  Length = 60
  MapMode = 5
  Placement = pos=(0,0,1.6) rot=(0,0,1;0rad)
  ResizeMode = 0
  Support = -> [XY_Plane011]
  Width = 60
FEATURE [PartDesign::Pad] Pad008  label="Photosensor_PCB_PCB"
  Direction = (1,1,1)
  Length = 10
  Length2 = 100
  Profile = -> Sketch020
  Type = 3
  UpToFace = -> DatumPlane005
FEATURE [Sketcher::SketchObject] Sketch021  label="Photosensor_PCB_Mounting_Hole_S"
  FullyConstrained = true
  MapMode = 5
  Placement = pos=(0,0,1.6) rot=(0,0,1;0rad)
  Support = -> [DatumPlane005]
  expr: Constraints[9] = Sketch020.Constraints[9]
  expr: Constraints[8] = Sketch020.Constraints[8]
  sketch-geometry (5):
    g0: LineSegment StartX=-7 StartY=15.5 StartZ=0 EndX=7 EndY=15.5 EndZ=0
    g1: LineSegment StartX=7 StartY=15.5 StartZ=0 EndX=7 EndY=-15.5 EndZ=0
    g2: LineSegment StartX=7 StartY=-15.5 StartZ=0 EndX=-7 EndY=-15.5 EndZ=0
    g3: LineSegment StartX=-7 StartY=-15.5 StartZ=0 EndX=-7 EndY=15.5 EndZ=0
    g4: Circle CenterX=0 CenterY=8.5 CenterZ=0 NormalX=0 NormalY=0 NormalZ=1 AngleXU=0 Radius=1.5
  constraints (13):
    c: Coincident(g0,g1)
    c: Coincident(g1,g2)
    c: Coincident(g2,g3)
    c: Coincident(g3,g0)
    c: Horizontal(g2)
    c: Vertical(g1)
    c: Symmetric(g0,g0,g-2)
    c: Symmetric(g0,g2,g-1)
    c: DistanceX(g0,g0) = 14
    c: DistanceY(g1,g1) = 31
    c: PointOnObject(g4,g-2)
    c: DistanceY(g4,g0) = 7
    c: Diameter(g4) = 3  'diameter'
FEATURE [PartDesign::Pocket] Pocket012  label="Photosensor_PCB_Mounting_Hole"
  BaseFeature = -> Pad008
  Length = 0
  Length2 = 100
  Profile = -> Sketch021
  Type = 3
  UpToFace = -> XY_Plane011
FEATURE [Sketcher::SketchObject] Sketch022  label="Photosensor_PCB_Adjust_Pot_S"
  FullyConstrained = true
  MapMode = 5
  Placement = pos=(0,0,1.6) rot=(0,0,1;0rad)
  Support = -> [DatumPlane005]
  expr: Constraints[9] = Sketch020.Constraints[9]
  expr: Constraints[8] = Sketch020.Constraints[8]
  sketch-geometry (5):
    g0: LineSegment StartX=-7 StartY=15.5 StartZ=0 EndX=7 EndY=15.5 EndZ=0
    g1: LineSegment StartX=7 StartY=15.5 StartZ=0 EndX=7 EndY=-15.5 EndZ=0
    g2: LineSegment StartX=7 StartY=-15.5 StartZ=0 EndX=-7 EndY=-15.5 EndZ=0
    g3: LineSegment StartX=-7 StartY=-15.5 StartZ=0 EndX=-7 EndY=15.5 EndZ=0
    g4: Circle CenterX=-3 CenterY=0 CenterZ=0 NormalX=0 NormalY=0 NormalZ=1 AngleXU=0 Radius=2.25
  constraints (13):
    c: Coincident(g0,g1)
    c: Coincident(g1,g2)
    c: Coincident(g2,g3)
    c: Coincident(g3,g0)
    c: Horizontal(g2)
    c: Vertical(g1)
    c: Symmetric(g0,g0,g-2)
    c: Symmetric(g0,g2,g-1)
    c: DistanceX(g0,g0) = 14
    c: DistanceY(g1,g1) = 31
    c: PointOnObject(g4,g-1)
    c: DistanceX(g4,g-1) = 3
    c: Diameter(g4) = 4.5
FEATURE [PartDesign::Pad] Pad009  label="Photosensor_PCB_Adjust_Pot"
  BaseFeature = -> Pocket012
  Direction = (1,1,1)
  Length = 1
  Length2 = 100
  Profile = -> Sketch022
  Type = 0
FEATURE [PartDesign::CoordinateSystem] Local_CS034  label="Photosensor_PCB_Mounting_Hole_Pos"
  AttacherType = Attacher::AttachEngine3D
  MapMode = 45
  Placement = pos=(7.1e-15,8.5,1.6) rot=(0,0,-1;0rad)
  Support = -> [Pad009]
FEATURE [PartDesign::Body] Photosensor_PCB
  Group = -> [Sketch020,DatumPlane005,Pad008,Sketch021,Pocket012,Sketch022,Pad009,Local_CS034]
  Origin = -> Origin011
  Tip = -> Pad009
COMPONENT P7 — recipe-attached ("Raspberry_Pi_3", modeled in this document).
Construction recipe (the document's own serialized feature program — sketch geometry with constraints, then the solid features built on it; lengths are millimeters unless a unit is written):

FEATURE [Sketcher::SketchObject] Sketch002
  FullyConstrained = true
  MapMode = 5
  Support = -> [XY_Plane002]
  sketch-geometry (8):
    g0: LineSegment StartX=-39.5 StartY=28 StartZ=0 EndX=39.5 EndY=28 EndZ=0
    g1: LineSegment StartX=42.5 StartY=25 StartZ=0 EndX=42.5 EndY=-25 EndZ=0
    g2: LineSegment StartX=39.5 StartY=-28 StartZ=0 EndX=-39.5 EndY=-28 EndZ=0
    g3: LineSegment StartX=-42.5 StartY=-25 StartZ=0 EndX=-42.5 EndY=25 EndZ=0
    g4: ArcOfCircle CenterX=-39.5 CenterY=25 CenterZ=0 NormalX=0 NormalY=0 NormalZ=1 AngleXU=0 Radius=3 StartAngle=1.5708 EndAngle=3.14159
    g5: ArcOfCircle CenterX=-39.5 CenterY=-25 CenterZ=0 NormalX=0 NormalY=0 NormalZ=1 AngleXU=0 Radius=3 StartAngle=3.14159 EndAngle=4.71239
    g6: ArcOfCircle CenterX=39.5 CenterY=-25 CenterZ=0 NormalX=0 NormalY=0 NormalZ=1 AngleXU=0 Radius=3 StartAngle=4.71239 EndAngle=6.28319
    g7: ArcOfCircle CenterX=39.5 CenterY=25 CenterZ=0 NormalX=0 NormalY=0 NormalZ=1 AngleXU=0 Radius=3 StartAngle=0 EndAngle=1.5708
  constraints (18):
    c: Horizontal(g0)
    c: Horizontal(g2)
    c: Vertical(g1)
    c: Vertical(g3)
    c: Tangent(g0,g4) = 1.5708
    c: Tangent(g3,g4) = 1.5708
    c: Tangent(g3,g5) = 1.5708
    c: Tangent(g2,g5) = 1.5708
    c: Tangent(g2,g6) = 1.5708
    c: Tangent(g1,g6) = 1.5708
    c: Tangent(g1,g7) = 1.5708
    c: Tangent(g0,g7) = 1.5708
    c: Equal(g5,g6)
    c: Radius(g7) = 3
    c: Symmetric(g0,g2,g-1)
    c: Symmetric(g3,g1,g-2)
    c: DistanceX(g3,g1) = 85
    c: DistanceY(g2,g0) = 56
FEATURE [PartDesign::Plane] DatumPlane001  label="Raspberry_Pi_3_Thickness"
  AttachmentOffset = pos=(0,0,1.6) rot=(0,0,1;0rad)
  Length = 98.7986
  MapMode = 5
  Placement = pos=(0,0,1.6) rot=(0,0,1;0rad)
  ResizeMode = 0
  Support = -> [XY_Plane002]
  Width = 69.7986
FEATURE [PartDesign::Pad] Pad001  label="Raspberry_Pi_3_PCB"
  Direction = (1,1,1)
  Length = 10
  Length2 = 100
  Profile = -> Sketch002
  Type = 3
  UpToFace = -> DatumPlane001 [Plane]
FEATURE [Sketcher::SketchObject] Sketch003
  FullyConstrained = true
  MapMode = 5
  Placement = pos=(0,0,1.6) rot=(0,0,1;0rad)
  Support = -> [DatumPlane001]
  expr: Constraints[35] = Sketch002.Constraints[17]
  expr: Constraints[34] = Sketch002.Constraints[16]
  expr: Constraints[31] = Sketch002.Constraints[13]
  sketch-geometry (16):
    g0: Circle CenterX=-39 CenterY=24.5 CenterZ=0 NormalX=0 NormalY=0 NormalZ=1 AngleXU=0 Radius=1.3
    g1: Circle CenterX=19 CenterY=24.5 CenterZ=0 NormalX=0 NormalY=0 NormalZ=1 AngleXU=0 Radius=1.3
    g2: Circle CenterX=-39 CenterY=-24.5 CenterZ=0 NormalX=0 NormalY=0 NormalZ=1 AngleXU=0 Radius=1.3
    g3: Circle CenterX=19 CenterY=-24.5 CenterZ=0 NormalX=0 NormalY=0 NormalZ=1 AngleXU=0 Radius=1.3
    g4: LineSegment StartX=-39 StartY=24.5 StartZ=0 EndX=19 EndY=24.5 EndZ=0
    g5: LineSegment StartX=19 StartY=24.5 StartZ=0 EndX=19 EndY=-24.5 EndZ=0
    g6: LineSegment StartX=19 StartY=-24.5 StartZ=0 EndX=-39 EndY=-24.5 EndZ=0
    g7: LineSegment StartX=-39 StartY=-24.5 StartZ=0 EndX=-39 EndY=24.5 EndZ=0
    g8: LineSegment StartX=-39.5 StartY=28 StartZ=0 EndX=39.5 EndY=28 EndZ=0
    g9: LineSegment StartX=42.5 StartY=25 StartZ=0 EndX=42.5 EndY=-25 EndZ=0
    g10: LineSegment StartX=39.5 StartY=-28 StartZ=0 EndX=-39.5 EndY=-28 EndZ=0
    g11: LineSegment StartX=-42.5 StartY=-25 StartZ=0 EndX=-42.5 EndY=25 EndZ=0
    g12: ArcOfCircle CenterX=-39.5 CenterY=25 CenterZ=0 NormalX=0 NormalY=0 NormalZ=1 AngleXU=0 Radius=3 StartAngle=1.5708 EndAngle=3.14159
    g13: ArcOfCircle CenterX=-39.5 CenterY=-25 CenterZ=0 NormalX=0 NormalY=0 NormalZ=1 AngleXU=0 Radius=3 StartAngle=3.14159 EndAngle=4.71239
    g14: ArcOfCircle CenterX=39.5 CenterY=-25 CenterZ=0 NormalX=0 NormalY=0 NormalZ=1 AngleXU=0 Radius=3 StartAngle=4.71239 EndAngle=6.28319
    g15: ArcOfCircle CenterX=39.5 CenterY=25 CenterZ=0 NormalX=0 NormalY=0 NormalZ=1 AngleXU=0 Radius=3 StartAngle=0 EndAngle=1.5708
  constraints (37):
    c: Equal(g0,g1)
    c: Equal(g1,g2)
    c: Equal(g2,g3)
    c: Diameter(g1) = 2.6  'hole_diameter'
    c: Coincident(g4,g5)
    c: Coincident(g5,g6)
    c: Coincident(g6,g7)
    c: Coincident(g7,g4)
    c: Horizontal(g4)
    c: Horizontal(g6)
    c: Vertical(g5)
    c: Symmetric(g4,g6,g-1)
    c: DistanceY(g7,g7) = 49
    c: DistanceX(g4,g4) = 58
    c: Coincident(g1,g4)
    c: Coincident(g3,g5)
    c: Coincident(g4,g0)
    c: Coincident(g6,g2)
    c: Horizontal(g8)
    c: Horizontal(g10)
    c: Vertical(g9)
    c: Vertical(g11)
    c: Tangent(g8,g12) = 1.5708
    c: Tangent(g11,g12) = 1.5708
    c: Tangent(g11,g13) = 1.5708
    c: Tangent(g10,g13) = 1.5708
    c: Tangent(g10,g14) = 1.5708
    c: Tangent(g9,g14) = 1.5708
    c: Tangent(g9,g15) = 1.5708
    c: Tangent(g8,g15) = 1.5708
    c: Equal(g13,g14)
    c: Radius(g15) = 3
    c: Symmetric(g8,g10,g-1)
    c: Symmetric(g11,g9,g-2)
    c: DistanceX(g11,g9) = 85
    c: DistanceY(g10,g8) = 56
    c: DistanceX(g11,g2) = 3.5
FEATURE [PartDesign::Pocket] Pocket001  label="Raspberry_Pi_3_Mounting_Holes"
  BaseFeature = -> Pad001
  Length = 0
  Length2 = 100
  Profile = -> Sketch003
  Type = 3
  UpToFace = -> XY_Plane002
FEATURE [PartDesign::CoordinateSystem] Local_CS003  label="Raspberry_Pi_3_Hole_1_Bottom"
  AttacherType = Attacher::AttachEngine3D
  MapMode = 45
  Placement = pos=(19,24.5,0) rot=(0,0,1;4.7e-05rad)
  Support = -> [Pocket001]
FEATURE [PartDesign::CoordinateSystem] Local_CS011  label="Raspberry_Pi_3_Hole_2_Bottom"
  AttacherType = Attacher::AttachEngine3D
  MapMode = 45
  Placement = pos=(-39,24.5,0) rot=(0,0,-1;5.6e-05rad)
  Support = -> [Pocket001]
FEATURE [PartDesign::CoordinateSystem] Local_CS012  label="Raspberry_Pi_3_Hole_3_Bottom"
  AttacherType = Attacher::AttachEngine3D
  MapMode = 45
  Placement = pos=(19,-24.5,0) rot=(0,0,-1;2.8e-05rad)
  Support = -> [Pocket001]
FEATURE [PartDesign::CoordinateSystem] Local_CS013  label="Raspberry_Pi_3_Hole_4_Bottom"
  AttacherType = Attacher::AttachEngine3D
  MapMode = 45
  Placement = pos=(-39,-24.5,0) rot=(0,0,1;1.9e-05rad)
  Support = -> [Pocket001]
FEATURE [PartDesign::Body] Raspberry_Pi_3
  Group = -> [DatumPlane001,Sketch002,Pad001,Sketch003,Pocket001,Local_CS003,Local_CS011,Local_CS012,Local_CS013]
  Origin = -> Origin002
  Tip = -> Pocket001
COMPONENT P8 — recipe-attached ("Raspberry_Pi_3_Standoff", modeled in this document).
Construction recipe (the document's own serialized feature program — sketch geometry with constraints, then the solid features built on it; lengths are millimeters unless a unit is written):

FEATURE [Sketcher::SketchObject] Sketch007
  FullyConstrained = true
  MapMode = 5
  Support = -> [XY_Plane005]
  expr: Constraints[2] = Sketch003.Constraints.hole_diameter
  sketch-geometry (2):
    g0: Circle CenterX=0 CenterY=0 CenterZ=0 NormalX=0 NormalY=0 NormalZ=1 AngleXU=0 Radius=2.5
    g1: Circle CenterX=0 CenterY=0 CenterZ=0 NormalX=0 NormalY=0 NormalZ=1 AngleXU=0 Radius=1.3
  constraints (4):
    c: Coincident(g0,g1)
    c: Coincident(g0,g-1)
    c: Diameter(g1) = 2.6
    c: Diameter(g0) = 5
FEATURE [PartDesign::Pad] Pad004  label="Raspberry_Pi_3_Standoff_Body"
  Direction = (1,1,1)
  Length = 3
  Length2 = 100
  Profile = -> Sketch007
  Type = 0
FEATURE [PartDesign::CoordinateSystem] Local_CS004  label="Raspberry_Pi_3_Standoff_Bottom"
  AttacherType = Attacher::AttachEngine3D
  MapMode = 45
  Placement = pos=(6.2e-15,1e-16,0) rot=(0,0,1;0rad)
  Support = -> [Pad004]
FEATURE [PartDesign::CoordinateSystem] Local_CS005  label="Raspberry_Pi_3_Standoff_Top"
  AttacherType = Attacher::AttachEngine3D
  MapMode = 45
  Placement = pos=(6.2e-15,1e-16,3) rot=(0,0,1;0rad)
  Support = -> [Pad004]
FEATURE [PartDesign::Body] Raspberry_Pi_3_standoff  label="Raspberry_Pi_3_Standoff"
  Group = -> [Sketch007,Pad004,Local_CS005,Local_CS004]
  Origin = -> Origin005
  Tip = -> Pad004
COMPONENT P9 — recipe-attached ("Relay_PCB", modeled in this document).
Construction recipe (the document's own serialized feature program — sketch geometry with constraints, then the solid features built on it; lengths are millimeters unless a unit is written):

FEATURE [Sketcher::SketchObject] Sketch
  FullyConstrained = true
  MapMode = 5
  Support = -> [XY_Plane001]
  sketch-geometry (4):
    g0: LineSegment StartX=-36 StartY=25.5 StartZ=0 EndX=36 EndY=25.5 EndZ=0
    g1: LineSegment StartX=36 StartY=25.5 StartZ=0 EndX=36 EndY=-25.5 EndZ=0
    g2: LineSegment StartX=36 StartY=-25.5 StartZ=0 EndX=-36 EndY=-25.5 EndZ=0
    g3: LineSegment StartX=-36 StartY=-25.5 StartZ=0 EndX=-36 EndY=25.5 EndZ=0
  constraints (10):
    c: Coincident(g0,g1)
    c: Coincident(g1,g2)
    c: Coincident(g2,g3)
    c: Coincident(g3,g0)
    c: Horizontal(g2)
    c: Vertical(g1)
    c: Symmetric(g0,g0,g-2)
    c: Symmetric(g0,g2,g-1)
    c: DistanceX(g0,g0) = 72
    c: DistanceY(g3,g3) = 51
FEATURE [PartDesign::Plane] DatumPlane  label="Relay_PCB_Thickness"
  AttachmentOffset = pos=(0,0,3) rot=(0,0,1;0rad)
  Length = 84.1194
  MapMode = 5
  Placement = pos=(0,0,3) rot=(0,0,1;0rad)
  ResizeMode = 0
  Support = -> [XY_Plane001]
  Width = 63.1194
FEATURE [PartDesign::Pad] Pad  label="Relay_PCB_PCB"
  Direction = (1,1,1)
  Length = 1.6
  Length2 = 100
  Profile = -> Sketch
  Type = 3
  UpToFace = -> DatumPlane [Plane]
FEATURE [Sketcher::SketchObject] Sketch001
  FullyConstrained = true
  MapMode = 5
  Placement = pos=(0,0,3) rot=(0,0,1;0rad)
  Support = -> [DatumPlane]
  sketch-geometry (8):
    g0: Circle CenterX=-33 CenterY=22.5 CenterZ=0 NormalX=0 NormalY=0 NormalZ=1 AngleXU=0 Radius=1.55
    g1: Circle CenterX=33 CenterY=22.5 CenterZ=0 NormalX=0 NormalY=0 NormalZ=1 AngleXU=0 Radius=1.55
    g2: Circle CenterX=-33 CenterY=-22.5 CenterZ=0 NormalX=0 NormalY=0 NormalZ=1 AngleXU=0 Radius=1.55
    g3: Circle CenterX=33 CenterY=-22.5 CenterZ=0 NormalX=0 NormalY=0 NormalZ=1 AngleXU=0 Radius=1.55
    g4: LineSegment StartX=-33 StartY=22.5 StartZ=0 EndX=33 EndY=22.5 EndZ=0
    g5: LineSegment StartX=33 StartY=22.5 StartZ=0 EndX=33 EndY=-22.5 EndZ=0
    g6: LineSegment StartX=33 StartY=-22.5 StartZ=0 EndX=-33 EndY=-22.5 EndZ=0
    g7: LineSegment StartX=-33 StartY=-22.5 StartZ=0 EndX=-33 EndY=22.5 EndZ=0
  constraints (18):
    c: Equal(g0,g1)
    c: Equal(g1,g2)
    c: Equal(g2,g3)
    c: Diameter(g1) = 3.1  'hole_diameter'
    c: Coincident(g4,g5)
    c: Coincident(g5,g6)
    c: Coincident(g6,g7)
    c: Coincident(g7,g4)
    c: Horizontal(g6)
    c: Vertical(g5)
    c: Symmetric(g4,g6,g-1)
    c: Symmetric(g4,g4,g-2)
    c: Coincident(g0,g4)
    c: Coincident(g2,g6)
    c: Coincident(g1,g4)
    c: Coincident(g3,g5)
    c: DistanceX(g4,g4) = 66
    c: DistanceY(g7,g7) = 45
FEATURE [PartDesign::Pocket] Pocket  label="Relay_PCB_Mounting_Holes"
  BaseFeature = -> Pad
  Length = 0
  Length2 = 100
  Profile = -> Sketch001
  Type = 3
  UpToFace = -> XY_Plane001
FEATURE [PartDesign::CoordinateSystem] Local_CS
  AttacherType = Attacher::AttachEngine3D
  MapMode = 45
  Placement = pos=(-33,-22.5,0) rot=(0,0,1;0rad)
  Support = -> [Pocket]
FEATURE [PartDesign::CoordinateSystem] Local_CS008
  AttacherType = Attacher::AttachEngine3D
  MapMode = 45
  Placement = pos=(-33,22.5,0) rot=(0,0,1;3.3e-05rad)
  Support = -> [Pocket]
FEATURE [PartDesign::CoordinateSystem] Local_CS009
  AttacherType = Attacher::AttachEngine3D
  MapMode = 45
  Placement = pos=(33,22.5,0) rot=(0,0,-1;1.1e-05rad)
  Support = -> [Pocket]
FEATURE [PartDesign::CoordinateSystem] Local_CS010
  AttacherType = Attacher::AttachEngine3D
  MapMode = 45
  Placement = pos=(33,-22.5,0) rot=(0,0,1;1.1e-05rad)
  Support = -> [Pocket]
FEATURE [PartDesign::Body] Relay_PCB
  Group = -> [DatumPlane,Sketch,Pad,Sketch001,Pocket,Local_CS,Local_CS008,Local_CS009,Local_CS010]
  Origin = -> Origin001
  Tip = -> Pocket
COMPONENT P10 — recipe-attached ("3mm_Standoff", modeled in this document).
Construction recipe (the document's own serialized feature program — sketch geometry with constraints, then the solid features built on it; lengths are millimeters unless a unit is written):

FEATURE [Sketcher::SketchObject] Sketch008
  FullyConstrained = true
  MapMode = 5
  Support = -> [XY_Plane006]
  sketch-geometry (2):
    g0: Circle CenterX=0 CenterY=0 CenterZ=0 NormalX=0 NormalY=0 NormalZ=1 AngleXU=0 Radius=3
    g1: Circle CenterX=0 CenterY=0 CenterZ=0 NormalX=0 NormalY=0 NormalZ=1 AngleXU=0 Radius=1.55
  constraints (4):
    c: Coincident(g0,g1)
    c: Coincident(g0,g-1)
    c: Diameter(g1) = 3.1
    c: Diameter(g0) = 6
FEATURE [PartDesign::Pad] Pad005  label="3mm_Standoff_Body"
  Direction = (1,1,1)
  Length = 3
  Length2 = 100
  Profile = -> Sketch008
  Type = 0
FEATURE [PartDesign::CoordinateSystem] Local_CS006  label="3mm_Standoff_Bottom"
  AttacherType = Attacher::AttachEngine3D
  MapMode = 45
  Placement = pos=(7.3e-15,0,0) rot=(0,0,1;0rad)
  Support = -> [Pad005]
FEATURE [PartDesign::CoordinateSystem] Local_CS007  label="3mm_Standoff_Top"
  AttacherType = Attacher::AttachEngine3D
  MapMode = 45
  Placement = pos=(7.3e-15,0,3) rot=(0,0,1;0rad)
  Support = -> [Pad005]
FEATURE [PartDesign::Body] Relay_PCB_standoff  label="3mm_Standoff"
  Group = -> [Sketch008,Pad005,Local_CS007,Local_CS006]
  Origin = -> Origin006
  Tip = -> Pad005
PROVENANCE & LICENSES
A FreeCAD (.FCStd) document from a public repository crawl; recipes are the document's own serialized feature recipes (and, for linked parts, companion documents' recipes).
License: mit.
